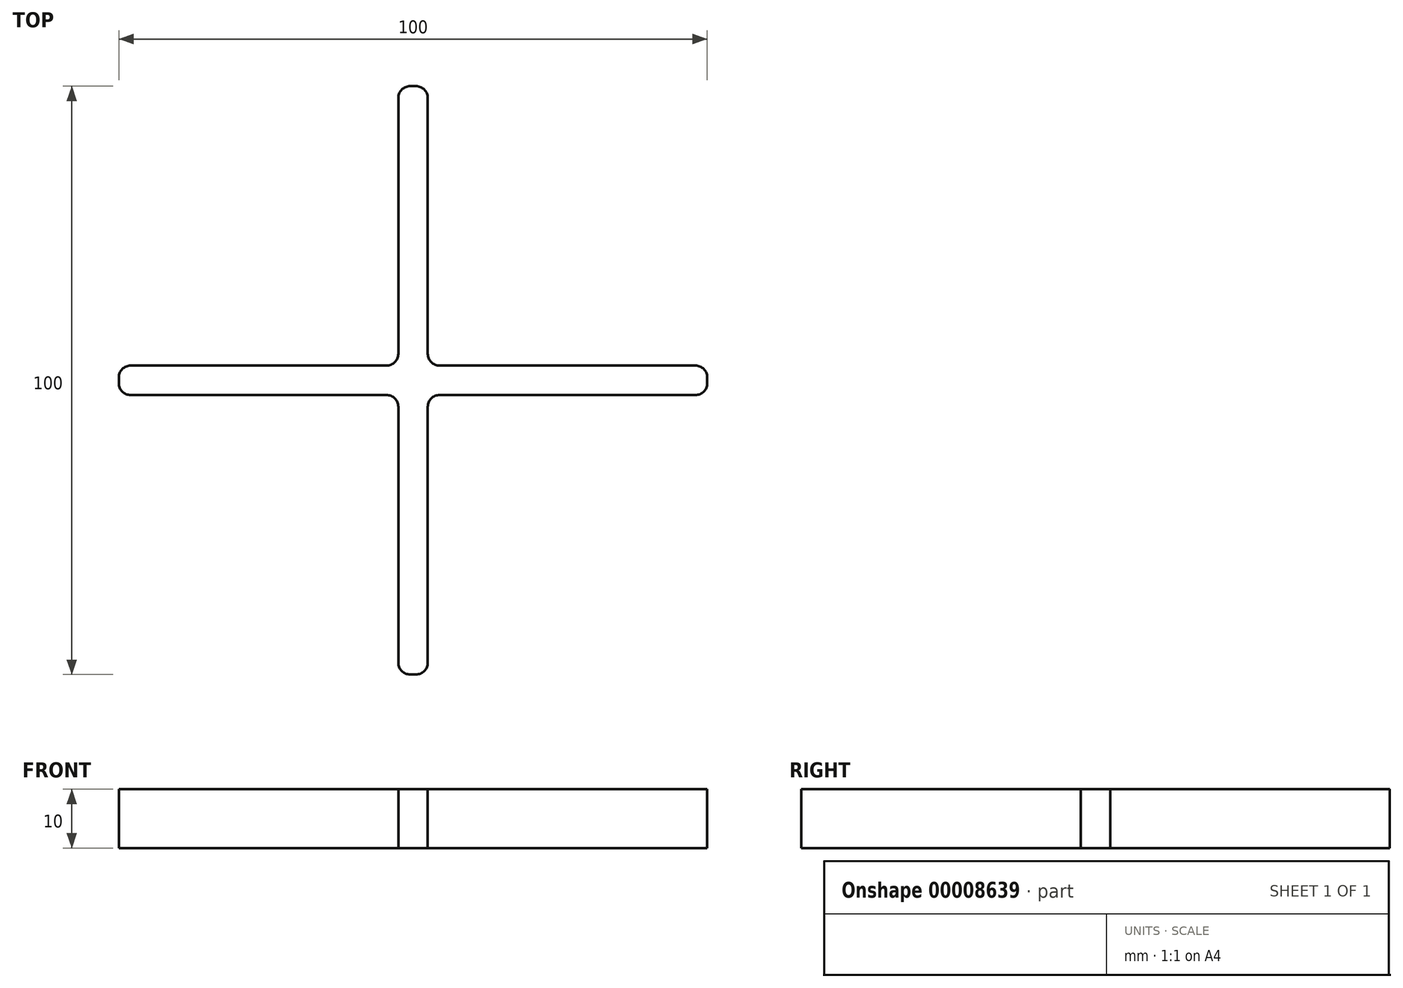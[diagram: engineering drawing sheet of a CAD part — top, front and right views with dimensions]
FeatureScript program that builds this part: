
annotation { "Feature Type Name" : "Feature", "Feature Type Description" : "" }
export const myFeature = defineFeature(function(context is Context, id is Id, definition is map)
    precondition{}
    {
        {
            var Q0;
            Q0=qCreatedBy(makeId("Top.planeOp"),FACE);
            var sketch = newSketch(context, id + "F0", { "sketchPlane" : qUnion([Q0])});
            skLineSegment(sketch, "E0.bottom", {"start": v(-50, 2.5) * mm, "end": v(50, 2.5) * mm});
            skLineSegment(sketch, "E0.top", {"start": v(-50, -2.5) * mm, "end": v(50, -2.5) * mm});
            skLineSegment(sketch, "E0.left", {"start": v(-50, 2.5) * mm, "end": v(-50, -2.5) * mm});
            skLineSegment(sketch, "E0.right", {"start": v(50, 2.5) * mm, "end": v(50, -2.5) * mm});
            skLineSegment(sketch, "E1.bottom", {"start": v(-2.5, 50) * mm, "end": v(2.5, 50) * mm});
            skLineSegment(sketch, "E1.top", {"start": v(-2.5, -50) * mm, "end": v(2.5, -50) * mm});
            skLineSegment(sketch, "E1.left", {"start": v(-2.5, 50) * mm, "end": v(-2.5, -50) * mm});
            skLineSegment(sketch, "E1.right", {"start": v(2.5, 50) * mm, "end": v(2.5, -50) * mm});
            skSolve(sketch);
        }
        {
            var Q0;
            {var subQ3=sQuery(id+"F0.wireOp",EDGE,"E1.bottom");Q0=makeQuery(id+"F0.imprint","IMPRINT",FACE,{"disambiguationData":[TD([[makeQuery(id+"F0.imprint","IMPRINT",EDGE,{"derivedFrom":subQ3}),-1.0]])]});}
            var Q1;
            {var subQ5=sQuery(id+"F0.wireOp",EDGE,"E0.left");Q1=makeQuery(id+"F0.imprint","IMPRINT",FACE,{"disambiguationData":[TD([[makeQuery(id+"F0.imprint","IMPRINT",EDGE,{"derivedFrom":subQ5}),1.0]])]});}
            var Q2;
            {var subQ5=sQuery(id+"F0.wireOp",EDGE,"E0.right");Q2=makeQuery(id+"F0.imprint","IMPRINT",FACE,{"disambiguationData":[TD([[makeQuery(id+"F0.imprint","IMPRINT",EDGE,{"derivedFrom":subQ5}),-1.0]])]});}
            var Q3;
            {var subQ3=sQuery(id+"F0.wireOp",EDGE,"E1.top");Q3=makeQuery(id+"F0.imprint","IMPRINT",FACE,{"disambiguationData":[TD([[makeQuery(id+"F0.imprint","IMPRINT",EDGE,{"derivedFrom":subQ3}),1.0]])]});}
            var Q4;
            {var subQ3=sQuery(id+"F0.wireOp",EDGE,"E0.bottom");var subQ5=sQuery(id+"F0.wireOp",EDGE,"E1.left");var subQ7=makeQuery(id+"F0.imprint","INTERSECT",VERTEX,{"derivedFrom":[subQ3,subQ5]});Q4=makeQuery(id+"F0.imprint","IMPRINT",FACE,{"disambiguationData":[TD([[makeQuery(id+"F0.imprint","IMPRINT",EDGE,{"disambiguationData":[TD([[subQ7,-1.0]])],"derivedFrom":subQ3}),-1.0]])]});}
            extrude(context, id + "F1", {"entities" : qUnion([Q0, Q1, Q2, Q3, Q4]), "depth" : 10 * mm});
        }
        {
            var Q0;
            Q0=makeQuery(id+"F1.opExtrude","SWEPT_EDGE",EDGE,{"disambiguationData":[OSD([sQuery(id+"F0.wireOp",EDGE,"E0.top"),sQuery(id+"F0.wireOp",EDGE,"E0.left")])]});
            var Q1;
            Q1=makeQuery(id+"F1.opExtrude","SWEPT_EDGE",EDGE,{"disambiguationData":[OSD([sQuery(id+"F0.wireOp",EDGE,"E1.top"),sQuery(id+"F0.wireOp",EDGE,"E1.left")])]});
            var Q2;
            Q2=makeQuery(id+"F1.opExtrude","SWEPT_EDGE",EDGE,{"disambiguationData":[OSD([sQuery(id+"F0.wireOp",EDGE,"E1.top"),sQuery(id+"F0.wireOp",EDGE,"E1.right")])]});
            var Q3;
            Q3=makeQuery(id+"F1.opExtrude","SWEPT_EDGE",EDGE,{"disambiguationData":[OSD([sQuery(id+"F0.wireOp",EDGE,"E0.top"),sQuery(id+"F0.wireOp",EDGE,"E0.right")])]});
            var Q4;
            Q4=makeQuery(id+"F1.opExtrude","SWEPT_EDGE",EDGE,{"disambiguationData":[OSD([sQuery(id+"F0.wireOp",EDGE,"E0.bottom"),sQuery(id+"F0.wireOp",EDGE,"E0.right")])]});
            var Q5;
            Q5=makeQuery(id+"F1.opExtrude","SWEPT_EDGE",EDGE,{"disambiguationData":[OSD([sQuery(id+"F0.wireOp",EDGE,"E1.bottom"),sQuery(id+"F0.wireOp",EDGE,"E1.right")])]});
            var Q6;
            Q6=makeQuery(id+"F1.opExtrude","SWEPT_EDGE",EDGE,{"disambiguationData":[OSD([sQuery(id+"F0.wireOp",EDGE,"E1.bottom"),sQuery(id+"F0.wireOp",EDGE,"E1.left")])]});
            var Q7;
            Q7=makeQuery(id+"F1.opExtrude","SWEPT_EDGE",EDGE,{"disambiguationData":[OSD([sQuery(id+"F0.wireOp",EDGE,"E0.bottom"),sQuery(id+"F0.wireOp",EDGE,"E0.left")])]});
            fillet(context, id + "F2", {"entities" : qUnion([Q0, Q1, Q2, Q3, Q4, Q5, Q6, Q7]), "radius" : 2 * mm, "tangentPropagation" : true, "allowEdgeOverflow" : false});
        }
        {
            var Q0;
            Q0=makeQuery(id+"F1.opExtrude","SWEPT_EDGE",EDGE,{"disambiguationData":[OSD([sQuery(id+"F0.wireOp",EDGE,"E0.top"),sQuery(id+"F0.wireOp",EDGE,"E1.right")])]});
            var Q1;
            Q1=makeQuery(id+"F1.opExtrude","SWEPT_EDGE",EDGE,{"disambiguationData":[OSD([sQuery(id+"F0.wireOp",EDGE,"E0.bottom"),sQuery(id+"F0.wireOp",EDGE,"E1.right")])]});
            var Q2;
            Q2=makeQuery(id+"F1.opExtrude","SWEPT_EDGE",EDGE,{"disambiguationData":[OSD([sQuery(id+"F0.wireOp",EDGE,"E0.bottom"),sQuery(id+"F0.wireOp",EDGE,"E1.left")])]});
            var Q3;
            Q3=makeQuery(id+"F1.opExtrude","SWEPT_EDGE",EDGE,{"disambiguationData":[OSD([sQuery(id+"F0.wireOp",EDGE,"E0.top"),sQuery(id+"F0.wireOp",EDGE,"E1.left")])]});
            fillet(context, id + "F3", {"entities" : qUnion([Q0, Q1, Q2, Q3]), "radius" : 2 * mm, "tangentPropagation" : true, "allowEdgeOverflow" : false});
        }
    });
